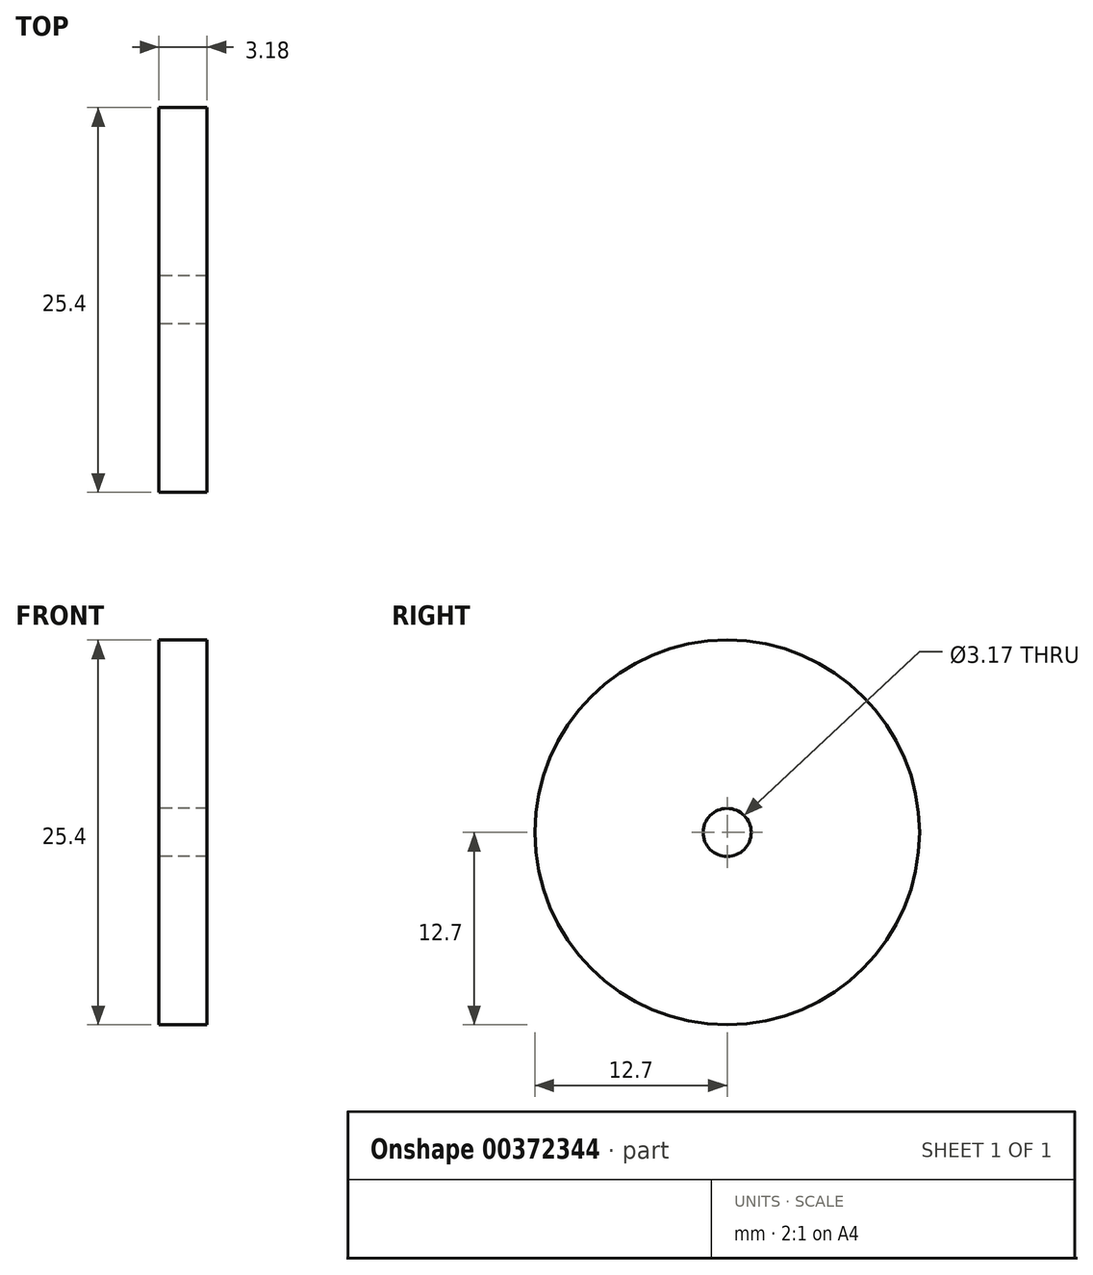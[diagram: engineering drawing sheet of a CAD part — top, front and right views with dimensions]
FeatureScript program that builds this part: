
annotation { "Feature Type Name" : "Feature", "Feature Type Description" : "" }
export const myFeature = defineFeature(function(context is Context, id is Id, definition is map)
    precondition{}
    {
        {
            var Q0;
            Q0=qCreatedBy(makeId("Right.planeOp"),FACE);
            var sketch = newSketch(context, id + "F0", { "sketchPlane" : qUnion([Q0])});
            skCircle(sketch, "E0", {"center": v(0, 0) * mm, "radius": 12.7 * mm});
            skCircle(sketch, "E1", {"center": v(0, 0) * mm, "radius": 1.59 * mm});
            skSolve(sketch);
        }
        {
            var Q0;
            Q0 = qSketchRegion(id + "F0", true);
            extrude(context, id + "F1", {"entities" : qUnion([Q0]), "endBound" : BoundingType.SYMMETRIC, "depth" : 3.17 * mm});
        }
    });
